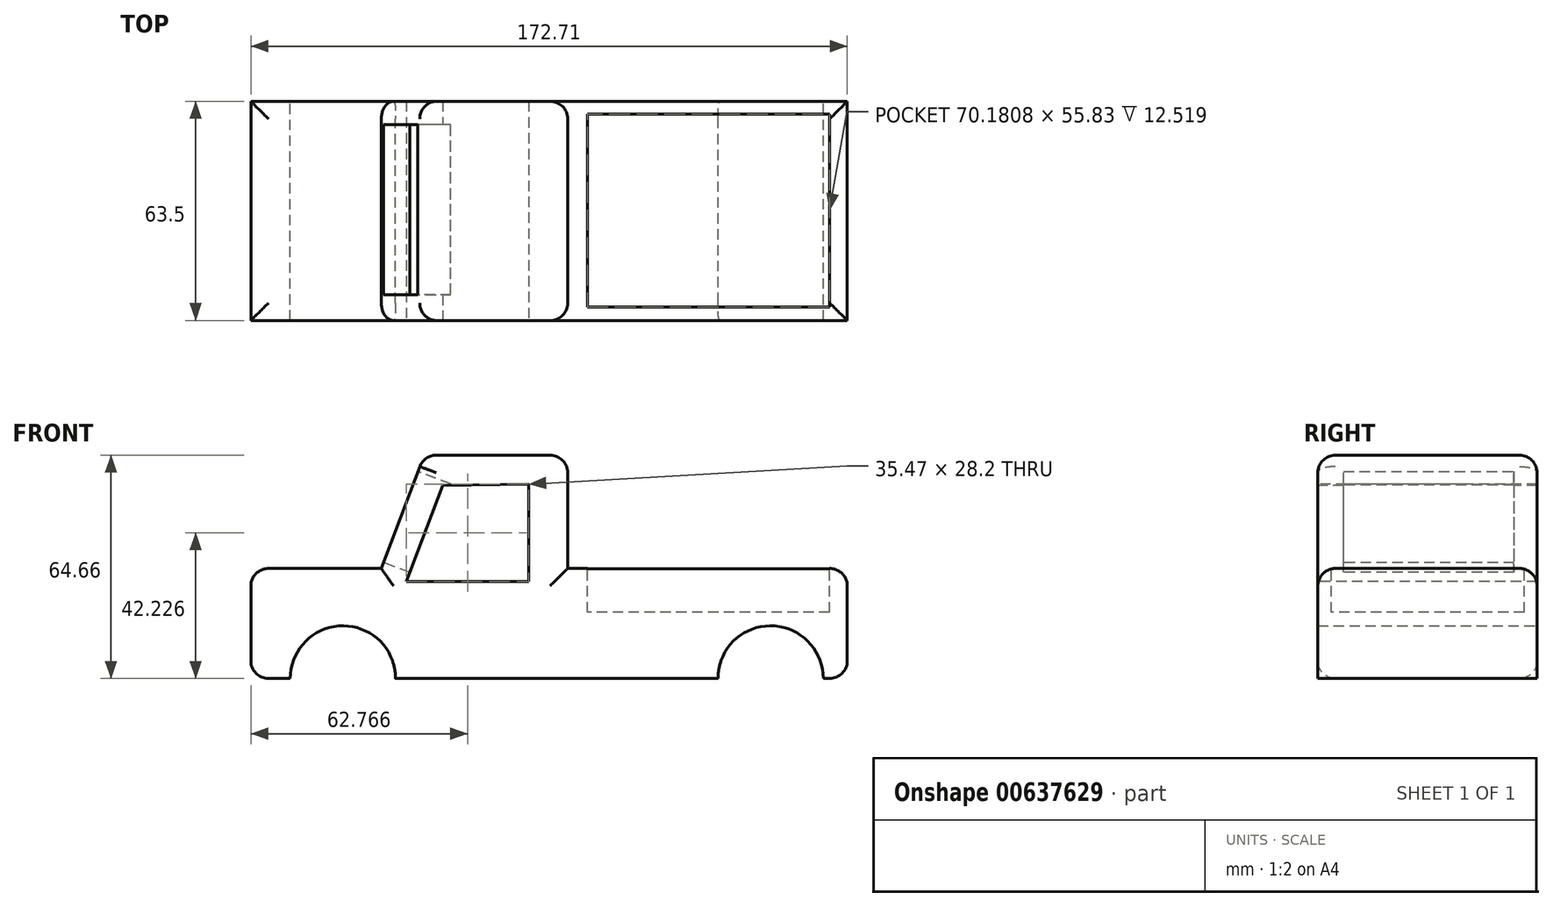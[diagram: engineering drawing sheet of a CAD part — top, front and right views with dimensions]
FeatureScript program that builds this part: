
annotation { "Feature Type Name" : "Feature", "Feature Type Description" : "" }
export const myFeature = defineFeature(function(context is Context, id is Id, definition is map)
    precondition{}
    {
        {
            var Q0;
            Q0=qCreatedBy(makeId("Front.planeOp"),FACE);
            var sketch = newSketch(context, id + "F0", { "sketchPlane" : qUnion([Q0])});
            skLineSegment(sketch, "E0", {"start": v(-60.58, -12.4) * mm, "end": v(-72.95, -12.4) * mm});
            skLineSegment(sketch, "E1", {"start": v(-72.95, -12.4) * mm, "end": v(-72.95, 19.47) * mm});
            skLineSegment(sketch, "E2", {"start": v(-72.95, 19.47) * mm, "end": v(-35.18, 19.47) * mm});
            skLineSegment(sketch, "E3", {"start": v(-35.18, 19.47) * mm, "end": v(-22.79, 52.27) * mm});
            skLineSegment(sketch, "E4", {"start": v(-22.79, 52.27) * mm, "end": v(18.78, 52.27) * mm});
            skLineSegment(sketch, "E5", {"start": v(18.78, 52.27) * mm, "end": v(18.78, 19.47) * mm});
            skLineSegment(sketch, "E6", {"start": v(18.78, 19.47) * mm, "end": v(99.76, 19.47) * mm});
            skLineSegment(sketch, "E7", {"start": v(99.76, 19.47) * mm, "end": v(99.76, -12.4) * mm});
            skArc(sketch, "E8", {"start": v(-31.05, -12.4) * mm, "mid": v(-46.3, 2.85) * mm, "end": v(-61.53, -12.4) * mm});
            skArc(sketch, "E9", {"start": v(92.8, -12.4) * mm, "mid": v(77.55, 2.85) * mm, "end": v(62.31, -12.4) * mm});
            skLineSegment(sketch, "E10.trimOffspring", {"start": v(-31.05, -12.4) * mm, "end": v(62.31, -12.4) * mm});
            skLineSegment(sketch, "E11.trimOffspring", {"start": v(92.8, -12.4) * mm, "end": v(99.76, -12.4) * mm});
            skSolve(sketch);
        }
        {
            var Q0;
            {var subQ1=sQuery(id+"F0.wireOp",EDGE,"E1");Q0=makeQuery(id+"F0.imprint","IMPRINT",FACE,{"disambiguationData":[TD([[makeQuery(id+"F0.imprint","IMPRINT",EDGE,{"derivedFrom":subQ1}),-1.0]])]});}
            extrude(context, id + "F1", {"entities" : qUnion([Q0]), "depth" : 63.5 * mm, "offsetDistance" : 25.4 * mm});
        }
        {
            var Q0;
            Q0=makeQuery(id+"F1.opExtrude","SWEPT_FACE",FACE,{"disambiguationData":[OSD([sQuery(id+"F0.wireOp",EDGE,"E6")])]});
            var sketch = newSketch(context, id + "F2", { "sketchPlane" : qUnion([Q0])});
            skLineSegment(sketch, "E12", {"start": v(24.46, -3.74) * mm, "end": v(24.46, -59.57) * mm});
            skLineSegment(sketch, "E13", {"start": v(24.46, -59.57) * mm, "end": v(94.64, -59.57) * mm});
            skLineSegment(sketch, "E14", {"start": v(94.64, -59.57) * mm, "end": v(94.64, -3.74) * mm});
            skLineSegment(sketch, "E15", {"start": v(94.64, -3.74) * mm, "end": v(24.46, -3.74) * mm});
            skSolve(sketch);
        }
        {
            var Q0;
            Q0=makeQuery(id+"F2.imprint","IMPRINT",FACE,{"disambiguationData":[TD([[makeQuery(id+"F2.imprint","IMPRINT",EDGE,{"derivedFrom":sQuery(id+"F2.wireOp",EDGE,"E12")}),1.0]])]});
            extrude(context, id + "F3", {"entities" : qUnion([Q0]), "operationType" : NewBodyOperationType.REMOVE, "oppositeDirection" : true, "depth" : 12.7 * mm, "offsetDistance" : 25.4 * mm});
        }
        {
            var Q0;
            Q0=makeQuery(id+"F1.opExtrude","CAP_EDGE",EDGE,{"disambiguationData":[OSD([sQuery(id+"F0.wireOp",EDGE,"E6")])],"isStart":false});
            var Q1;
            Q1=makeQuery(id+"F1.opExtrude","SWEPT_EDGE",EDGE,{"disambiguationData":[OSD([sQuery(id+"F0.wireOp",EDGE,"E6"),sQuery(id+"F0.wireOp",EDGE,"E7")])]});
            var Q2;
            Q2=makeQuery(id+"F1.opExtrude","CAP_EDGE",EDGE,{"disambiguationData":[OSD([sQuery(id+"F0.wireOp",EDGE,"E6")])],"isStart":true});
            var Q3;
            Q3=makeQuery(id+"F1.opExtrude","CAP_EDGE",EDGE,{"disambiguationData":[OSD([sQuery(id+"F0.wireOp",EDGE,"E10.trimOffspring")])],"isStart":true});
            var Q4;
            Q4=makeQuery(id+"F1.opExtrude","SWEPT_EDGE",EDGE,{"disambiguationData":[OSD([sQuery(id+"F0.wireOp",EDGE,"E7"),sQuery(id+"F0.wireOp",EDGE,"E11.trimOffspring")])]});
            var Q5;
            Q5=makeQuery(id+"F1.opExtrude","CAP_EDGE",EDGE,{"disambiguationData":[OSD([sQuery(id+"F0.wireOp",EDGE,"E10.trimOffspring")])],"isStart":false});
            var Q6;
            Q6=makeQuery(id+"F1.opExtrude","CAP_EDGE",EDGE,{"disambiguationData":[OSD([sQuery(id+"F0.wireOp",EDGE,"E2")])],"isStart":false});
            var Q7;
            Q7=makeQuery(id+"F1.opExtrude","SWEPT_EDGE",EDGE,{"disambiguationData":[OSD([sQuery(id+"F0.wireOp",EDGE,"E1"),sQuery(id+"F0.wireOp",EDGE,"E2")])]});
            var Q8;
            Q8=makeQuery(id+"F1.opExtrude","CAP_EDGE",EDGE,{"disambiguationData":[OSD([sQuery(id+"F0.wireOp",EDGE,"E2")])],"isStart":true});
            var Q9;
            Q9=makeQuery(id+"F1.opExtrude","SWEPT_EDGE",EDGE,{"disambiguationData":[OSD([sQuery(id+"F0.wireOp",EDGE,"E0"),sQuery(id+"F0.wireOp",EDGE,"E1")])]});
            var Q10;
            Q10=makeQuery(id+"F1.opExtrude","SWEPT_EDGE",EDGE,{"disambiguationData":[OSD([sQuery(id+"F0.wireOp",EDGE,"E3"),sQuery(id+"F0.wireOp",EDGE,"E4")])]});
            var Q11;
            Q11=makeQuery(id+"F1.opExtrude","SWEPT_EDGE",EDGE,{"disambiguationData":[OSD([sQuery(id+"F0.wireOp",EDGE,"E4"),sQuery(id+"F0.wireOp",EDGE,"E5")])]});
            var Q12;
            Q12=makeQuery(id+"F1.opExtrude","CAP_EDGE",EDGE,{"disambiguationData":[OSD([sQuery(id+"F0.wireOp",EDGE,"E3")])],"isStart":false});
            var Q13;
            Q13=makeQuery(id+"F1.opExtrude","CAP_EDGE",EDGE,{"disambiguationData":[OSD([sQuery(id+"F0.wireOp",EDGE,"E3")])],"isStart":true});
            fillet(context, id + "F4", {"entities" : qUnion([Q0, Q1, Q2, Q3, Q4, Q5, Q6, Q7, Q8, Q9, Q10, Q11, Q12, Q13]), "radius" : 5.08 * mm, "tangentPropagation" : true, "allowEdgeOverflow" : false});
        }
        {
            var Q0;
            {var subQ0=sQuery(id+"F0.wireOp",EDGE,"E5");var subQ1=sQuery(id+"F0.wireOp",EDGE,"E4");Q0=makeQuery(id+"F4.opFillet","BLEND_EDGE",EDGE,{"blendedFrom":[makeQuery(id+"F1.opExtrude","SWEPT_EDGE",EDGE,{"disambiguationData":[OSD([subQ1,subQ0])]}),makeQuery(id+"F1.opExtrude","CAP_FACE",FACE,{"disambiguationData":[OSD([sQuery(id+"F0.wireOp",EDGE,"E0"),sQuery(id+"F0.wireOp",EDGE,"E1"),sQuery(id+"F0.wireOp",EDGE,"E2"),sQuery(id+"F0.wireOp",EDGE,"E3"),subQ1,subQ0,sQuery(id+"F0.wireOp",EDGE,"E6"),sQuery(id+"F0.wireOp",EDGE,"E7"),sQuery(id+"F0.wireOp",EDGE,"E8"),sQuery(id+"F0.wireOp",EDGE,"E9"),sQuery(id+"F0.wireOp",EDGE,"E10.trimOffspring"),sQuery(id+"F0.wireOp",EDGE,"E11.trimOffspring")])],"isStart":false})],"blendedInto":[makeQuery(id+"F1.opExtrude","CAP_FACE",FACE,{"disambiguationData":[OSD([sQuery(id+"F0.wireOp",EDGE,"E0"),sQuery(id+"F0.wireOp",EDGE,"E1"),sQuery(id+"F0.wireOp",EDGE,"E2"),sQuery(id+"F0.wireOp",EDGE,"E3"),subQ1,subQ0,sQuery(id+"F0.wireOp",EDGE,"E6"),sQuery(id+"F0.wireOp",EDGE,"E7"),sQuery(id+"F0.wireOp",EDGE,"E8"),sQuery(id+"F0.wireOp",EDGE,"E9"),sQuery(id+"F0.wireOp",EDGE,"E10.trimOffspring"),sQuery(id+"F0.wireOp",EDGE,"E11.trimOffspring")])],"isStart":false})]});}
            fillet(context, id + "F5", {"entities" : qUnion([Q0]), "radius" : 5.08 * mm, "tangentPropagation" : true, "allowEdgeOverflow" : false});
        }
        {
            var Q0;
            Q0=makeQuery(id+"F1.opExtrude","CAP_EDGE",EDGE,{"disambiguationData":[OSD([sQuery(id+"F0.wireOp",EDGE,"E5")])],"isStart":true});
            fillet(context, id + "F6", {"entities" : qUnion([Q0]), "radius" : 5.08 * mm, "tangentPropagation" : true, "allowEdgeOverflow" : false});
        }
        {
            var Q0;
            Q0=makeQuery(id+"F1.opExtrude","CAP_FACE",FACE,{"disambiguationData":[OSD([sQuery(id+"F0.wireOp",EDGE,"E0"),sQuery(id+"F0.wireOp",EDGE,"E1"),sQuery(id+"F0.wireOp",EDGE,"E2"),sQuery(id+"F0.wireOp",EDGE,"E3"),sQuery(id+"F0.wireOp",EDGE,"E4"),sQuery(id+"F0.wireOp",EDGE,"E5"),sQuery(id+"F0.wireOp",EDGE,"E6"),sQuery(id+"F0.wireOp",EDGE,"E7"),sQuery(id+"F0.wireOp",EDGE,"E8"),sQuery(id+"F0.wireOp",EDGE,"E9"),sQuery(id+"F0.wireOp",EDGE,"E10.trimOffspring"),sQuery(id+"F0.wireOp",EDGE,"E11.trimOffspring")])],"isStart":false});
            var sketch = newSketch(context, id + "F7", { "sketchPlane" : qUnion([Q0])});
            skLineSegment(sketch, "E16", {"start": v(-17.41, 43.54) * mm, "end": v(-27.92, 15.74) * mm});
            skLineSegment(sketch, "E17", {"start": v(-27.92, 15.74) * mm, "end": v(7.55, 15.74) * mm});
            skLineSegment(sketch, "E18", {"start": v(7.55, 15.74) * mm, "end": v(7.55, 43.94) * mm});
            skLineSegment(sketch, "E19", {"start": v(7.55, 43.94) * mm, "end": v(-17.41, 43.54) * mm});
            skSolve(sketch);
        }
        {
            var Q0;
            Q0=makeQuery(id+"F7.imprint","IMPRINT",FACE,{"disambiguationData":[TD([[makeQuery(id+"F7.imprint","IMPRINT",EDGE,{"derivedFrom":sQuery(id+"F7.wireOp",EDGE,"E16")}),1.0]])]});
            extrude(context, id + "F8", {"entities" : qUnion([Q0]), "operationType" : NewBodyOperationType.REMOVE, "oppositeDirection" : true, "depth" : 101.6 * mm, "offsetDistance" : 25.4 * mm});
        }
        {
            var Q0;
            Q0=makeQuery(id+"F1.opExtrude","SWEPT_FACE",FACE,{"disambiguationData":[OSD([sQuery(id+"F0.wireOp",EDGE,"E3")])]});
            var sketch = newSketch(context, id + "F9", { "sketchPlane" : qUnion([Q0])});
            skLineSegment(sketch, "E20", {"start": v(6.72, 35.77) * mm, "end": v(6.72, 7.59) * mm});
            skLineSegment(sketch, "E21", {"start": v(6.72, 7.59) * mm, "end": v(56.03, 7.59) * mm});
            skLineSegment(sketch, "E22", {"start": v(56.03, 7.59) * mm, "end": v(56.03, 35.8) * mm});
            skLineSegment(sketch, "E23", {"start": v(56.03, 35.8) * mm, "end": v(6.72, 35.77) * mm});
            skSolve(sketch);
        }
        {
            var Q0;
            Q0=makeQuery(id+"F9.imprint","IMPRINT",FACE,{"disambiguationData":[TD([[makeQuery(id+"F9.imprint","IMPRINT",EDGE,{"derivedFrom":sQuery(id+"F9.wireOp",EDGE,"E20")}),1.0]])]});
            extrude(context, id + "F10", {"entities" : qUnion([Q0]), "operationType" : NewBodyOperationType.REMOVE, "oppositeDirection" : true, "depth" : 10.16 * mm, "offsetDistance" : 25.4 * mm});
        }
    });
